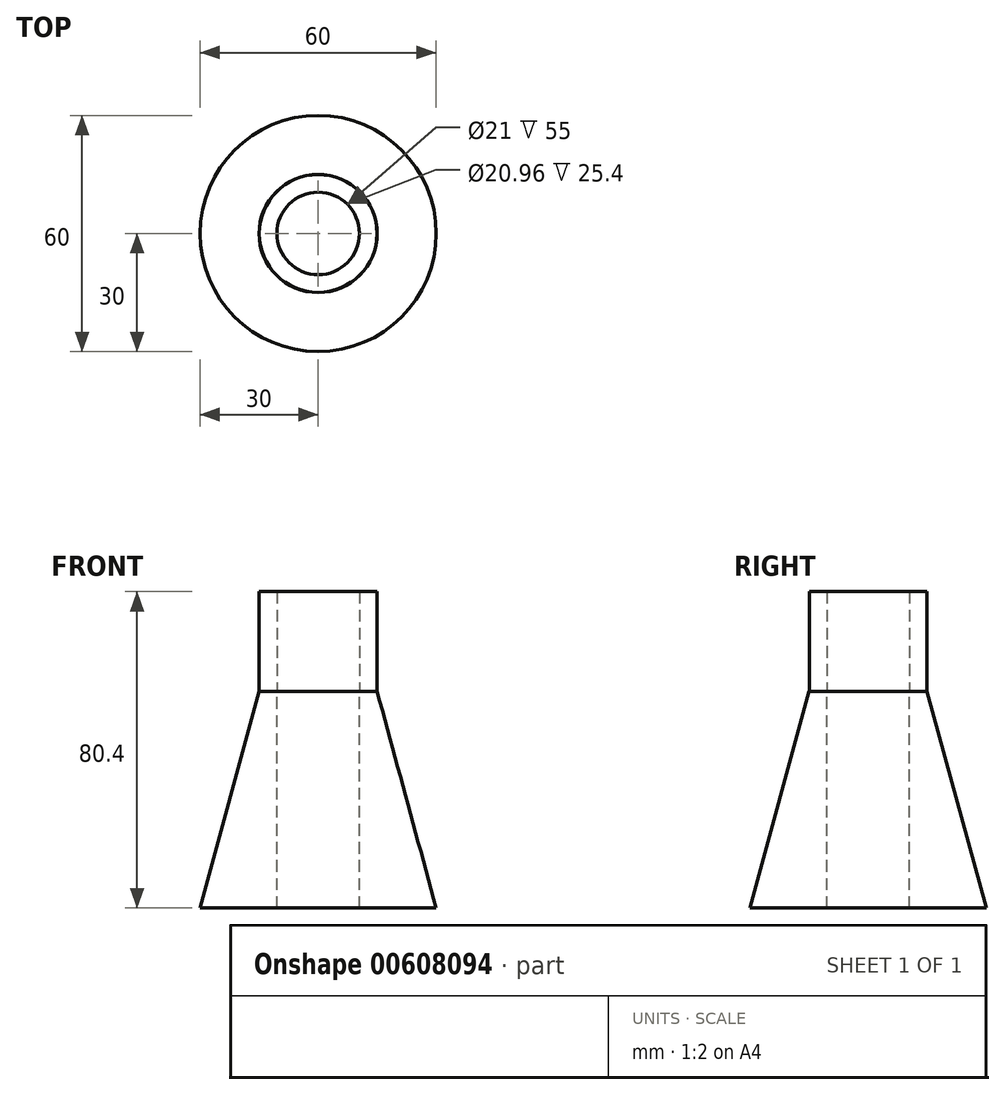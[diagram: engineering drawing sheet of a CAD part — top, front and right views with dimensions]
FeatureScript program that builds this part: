
annotation { "Feature Type Name" : "Feature", "Feature Type Description" : "" }
export const myFeature = defineFeature(function(context is Context, id is Id, definition is map)
    precondition{}
    {
        {
            var Q0;
            Q0=qCreatedBy(makeId("Front.planeOp"),FACE);
            var sketch = newSketch(context, id + "F0", { "sketchPlane" : qUnion([Q0])});
            skLineSegment(sketch, "E0", {"start": v(0, 4.27) * mm, "end": v(0, -50.73) * mm});
            skLineSegment(sketch, "E1", {"start": v(0, -50.73) * mm, "end": v(-30, -50.73) * mm});
            skLineSegment(sketch, "E2", {"start": v(-30, -50.73) * mm, "end": v(-15, 4.27) * mm});
            skLineSegment(sketch, "E3", {"start": v(-15, 4.27) * mm, "end": v(0, 4.27) * mm});
            skSolve(sketch);
        }
        {
            var Q0;
            Q0=makeQuery(id+"F0.imprint","IMPRINT",FACE,{"disambiguationData":[TD([[makeQuery(id+"F0.imprint","IMPRINT",EDGE,{"derivedFrom":sQuery(id+"F0.wireOp",EDGE,"E0")}),-1.0]])]});
            var Q1;
            Q1=sQuery(id+"F0.wireOp",EDGE,"E0");
            revolve(context, id + "F1", {"entities" : qUnion([Q0]), "axis" : qUnion([Q1]), "revolveType" : RevolveType.FULL});
        }
        {
            var Q0;
            Q0=makeQuery(id+"F1.opRevolve","SWEPT_FACE",FACE,{"disambiguationData":[OSD([sQuery(id+"F0.wireOp",EDGE,"E3")])]});
            var sketch = newSketch(context, id + "F2", { "sketchPlane" : qUnion([Q0])});
            skCircle(sketch, "E4", {"center": v(0, 0) * mm, "radius": 10.5 * mm});
            skSolve(sketch);
        }
        {
            var Q0;
            Q0=makeQuery(id+"F2.imprint","IMPRINT",FACE,{"disambiguationData":[TD([[makeQuery(id+"F2.imprint","IMPRINT",EDGE,{"derivedFrom":sQuery(id+"F2.wireOp",EDGE,"E4")}),1.0]])]});
            extrude(context, id + "F3", {"entities" : qUnion([Q0]), "operationType" : NewBodyOperationType.REMOVE, "oppositeDirection" : true, "depth" : 90.17 * mm, "offsetDistance" : 25.4 * mm});
        }
        {
            var Q0;
            Q0=makeQuery(id+"F1.opRevolve","SWEPT_FACE",FACE,{"disambiguationData":[OSD([sQuery(id+"F0.wireOp",EDGE,"E3")])]});
            var sketch = newSketch(context, id + "F4", { "sketchPlane" : qUnion([Q0])});
            skCircle(sketch, "E5", {"center": v(0, 0) * mm, "radius": 10.48 * mm});
            skCircle(sketch, "E6", {"center": v(0, 0) * mm, "radius": 14.96 * mm});
            skSolve(sketch);
        }
        {
            var Q0;
            Q0 = qSketchRegion(id + "F4", true);
            extrude(context, id + "F5", {"entities" : qUnion([Q0]), "operationType" : NewBodyOperationType.ADD, "depth" : 25.4 * mm, "offsetDistance" : 25.4 * mm});
        }
    });
